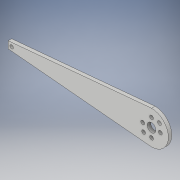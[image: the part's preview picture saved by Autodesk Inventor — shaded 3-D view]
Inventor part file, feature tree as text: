
AUTODESK INVENTOR PART (.ipt)
format: ipt  version: 2017 (Build 210142000, 142)  size: 187,904 bytes
history: native  units: in
note: dims shown in document units (in); Inventor stores cm internally (conversion verified against a paired STEP export)
features: extrude x11, sketch x9, plane x1
ambient origin geometry x8: Origin, YZ Plane, XZ Plane, XY Plane, X Axis, Y Axis, Z Axis, Center Point
bodies: Solid1 (feature_tree)
feature tree (21):
  sketch  "Sketch1"  dims[d0=1.2in d1=0.125in d2=0.0in]
  extrude  "Extrusion1"  Depth=0.125in TaperAngle=0.0deg
  sketch  "Sketch2"  dims[d3=0.125in d4=0.125in]
  plane  "Work Plane1"
  extrude  "Extrusion2"  Depth=0.125in
  extrude  "Extrusion3"  Depth=4.5295in TaperAngle=0.0deg
  extrude  "Extrusion4"  Depth=0.315in
  extrude  "Extrusion5"  Depth=0.315in
  extrude  "Extrusion7"  Depth=0.315in
  extrude  "Extrusion9"  Depth=0.138in
  sketch  "Sketch11"  dims[d18=0.138in d19=0.5in d20=0.0in]
  extrude  "Extrusion11"  Depth=0.5in TaperAngle=0.0deg
  extrude  "Extrusion12"  Depth=0.125in TaperAngle=0.0deg
  sketch  "Sketch12"  dims[d21=0.314in d22=0.5in d23=0.0in d26=0.125in d27=0.125in d28=0.125in d29=0.0in d37=0.4in d38=45.0deg d39=0.4in d40=0.138in d41=0.138in d42=1.0in d43=0.0in d47=1.0in d48=1.0in d49=0.0in d50=1.0in d51=1.0in d52=0.0in d53=0.125in d54=0.0in d55=0.125in d56=0.0in]
  extrude  "Extrusion13"  Depth=0.125in
  extrude  "Extrusion14"  Depth=0.125in
  sketch  "Sketch3"  dims[d6=0.25in d7=4.5295in d8=0.0in]
  sketch  "Sketch4"  dims[d9=0.5in d10=0.0in d11=0.315in]
  sketch  "Sketch5"  dims[d12=0.315in d13=0.315in]
  sketch  "Sketch7"  dims[d14=0.315in d15=0.138in]
  sketch  "Sketch9"  dims[d16=0.138in d17=0.138in]
